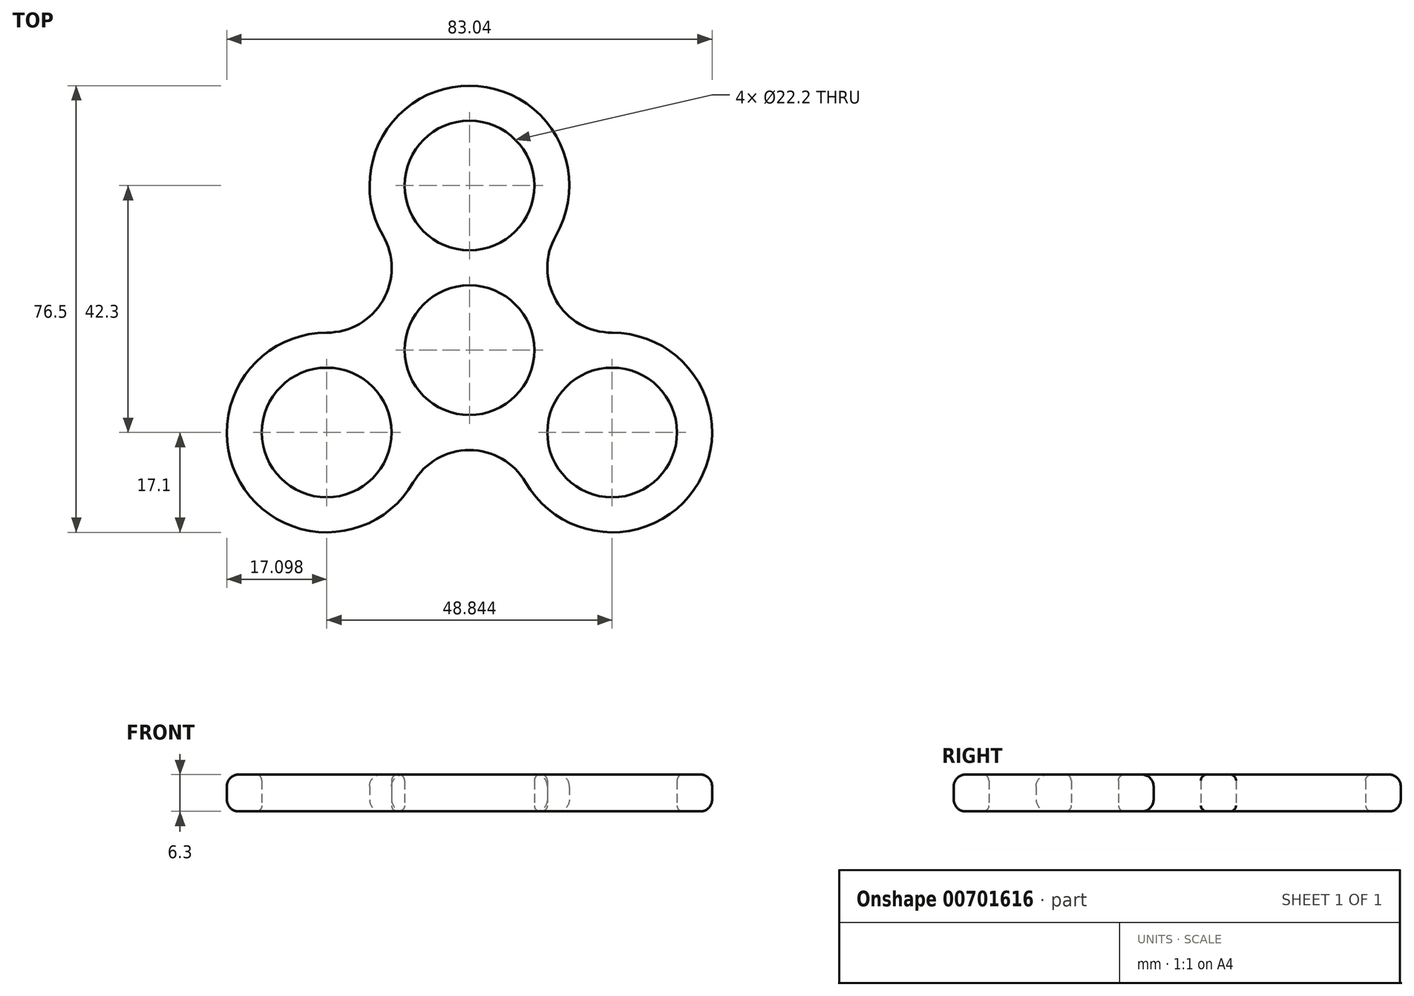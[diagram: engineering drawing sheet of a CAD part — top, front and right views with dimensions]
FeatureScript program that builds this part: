
annotation { "Feature Type Name" : "Feature", "Feature Type Description" : "" }
export const myFeature = defineFeature(function(context is Context, id is Id, definition is map)
    precondition{}
    {
        {
            var Q0;
            Q0=qCreatedBy(makeId("Top.planeOp"),FACE);
            var sketch = newSketch(context, id + "F0", { "sketchPlane" : qUnion([Q0])});
            skCircle(sketch, "E0", {"center": v(0, 0) * mm, "radius": 11.1 * mm});
            skCircle(sketch, "E1", {"center": v(0, 28.2) * mm, "radius": 11.1 * mm});
            skArc(sketch, "E2.0", {"start": v(14.8, 19.65) * mm, "mid": v(0, 45.3) * mm, "end": v(-14.8, 19.65) * mm});
            skArc(sketch, "E3.1.0", {"start": v(-24.42, 3) * mm, "mid": v(-39.23, -22.65) * mm, "end": v(-9.61, -22.65) * mm});
            skCircle(sketch, "E3.1.1", {"center": v(-24.42, -14.1) * mm, "radius": 11.1 * mm});
            skArc(sketch, "E3.2.0", {"start": v(9.61, -22.65) * mm, "mid": v(39.23, -22.65) * mm, "end": v(24.42, 3) * mm});
            skCircle(sketch, "E3.2.1", {"center": v(24.42, -14.1) * mm, "radius": 11.1 * mm});
            skArc(sketch, "E4", {"start": v(14.8, 19.65) * mm, "mid": v(14.8, 8.55) * mm, "end": v(24.42, 3) * mm});
            skArc(sketch, "E5.1.0", {"start": v(-24.42, 3) * mm, "mid": v(-14.8, 8.55) * mm, "end": v(-14.8, 19.65) * mm});
            skArc(sketch, "E5.2.0", {"start": v(9.61, -22.65) * mm, "mid": v(0, -17.1) * mm, "end": v(-9.61, -22.65) * mm});
            skSolve(sketch);
        }
        {
            var Q0;
            Q0=makeQuery(id+"F0.imprint","IMPRINT",FACE,{"disambiguationData":[TD([[makeQuery(id+"F0.imprint","IMPRINT",EDGE,{"derivedFrom":sQuery(id+"F0.wireOp",EDGE,"E0")}),-1.0]])]});
            extrude(context, id + "F1", {"entities" : qUnion([Q0]), "depth" : 6.3 * mm, "offsetDistance" : 25 * mm});
        }
        {
            var Q0;
            Q0=makeQuery(id+"F1.opExtrude","CAP_EDGE",EDGE,{"disambiguationData":[OSD([sQuery(id+"F0.wireOp",EDGE,"E5.1.0")])],"isStart":false});
            var Q1;
            Q1=makeQuery(id+"F1.opExtrude","CAP_EDGE",EDGE,{"disambiguationData":[OSD([sQuery(id+"F0.wireOp",EDGE,"E3.1.0")])],"isStart":true});
            fillet(context, id + "F2", {"entities" : qUnion([Q0, Q1]), "radius" : 2 * mm, "tangentPropagation" : true, "allowEdgeOverflow" : false});
        }
        {
            var Q0;
            Q0=makeQuery(id+"F1.opExtrude","CAP_EDGE",EDGE,{"disambiguationData":[OSD([sQuery(id+"F0.wireOp",EDGE,"E3.1.1")])],"isStart":true});
            var Q1;
            Q1=makeQuery(id+"F1.opExtrude","CAP_EDGE",EDGE,{"disambiguationData":[OSD([sQuery(id+"F0.wireOp",EDGE,"E0")])],"isStart":true});
            var Q2;
            Q2=makeQuery(id+"F1.opExtrude","CAP_EDGE",EDGE,{"disambiguationData":[OSD([sQuery(id+"F0.wireOp",EDGE,"E3.2.1")])],"isStart":true});
            var Q3;
            Q3=makeQuery(id+"F1.opExtrude","CAP_EDGE",EDGE,{"disambiguationData":[OSD([sQuery(id+"F0.wireOp",EDGE,"E1")])],"isStart":true});
            var Q4;
            Q4=makeQuery(id+"F1.opExtrude","CAP_EDGE",EDGE,{"disambiguationData":[OSD([sQuery(id+"F0.wireOp",EDGE,"E0")])],"isStart":false});
            var Q5;
            Q5=makeQuery(id+"F1.opExtrude","CAP_EDGE",EDGE,{"disambiguationData":[OSD([sQuery(id+"F0.wireOp",EDGE,"E3.2.1")])],"isStart":false});
            var Q6;
            Q6=makeQuery(id+"F1.opExtrude","CAP_EDGE",EDGE,{"disambiguationData":[OSD([sQuery(id+"F0.wireOp",EDGE,"E1")])],"isStart":false});
            var Q7;
            Q7=makeQuery(id+"F1.opExtrude","CAP_EDGE",EDGE,{"disambiguationData":[OSD([sQuery(id+"F0.wireOp",EDGE,"E3.1.1")])],"isStart":false});
            fillet(context, id + "F3", {"entities" : qUnion([Q0, Q1, Q2, Q3, Q4, Q5, Q6, Q7]), "radius" : 1 * mm, "tangentPropagation" : true, "allowEdgeOverflow" : false});
        }
    });
